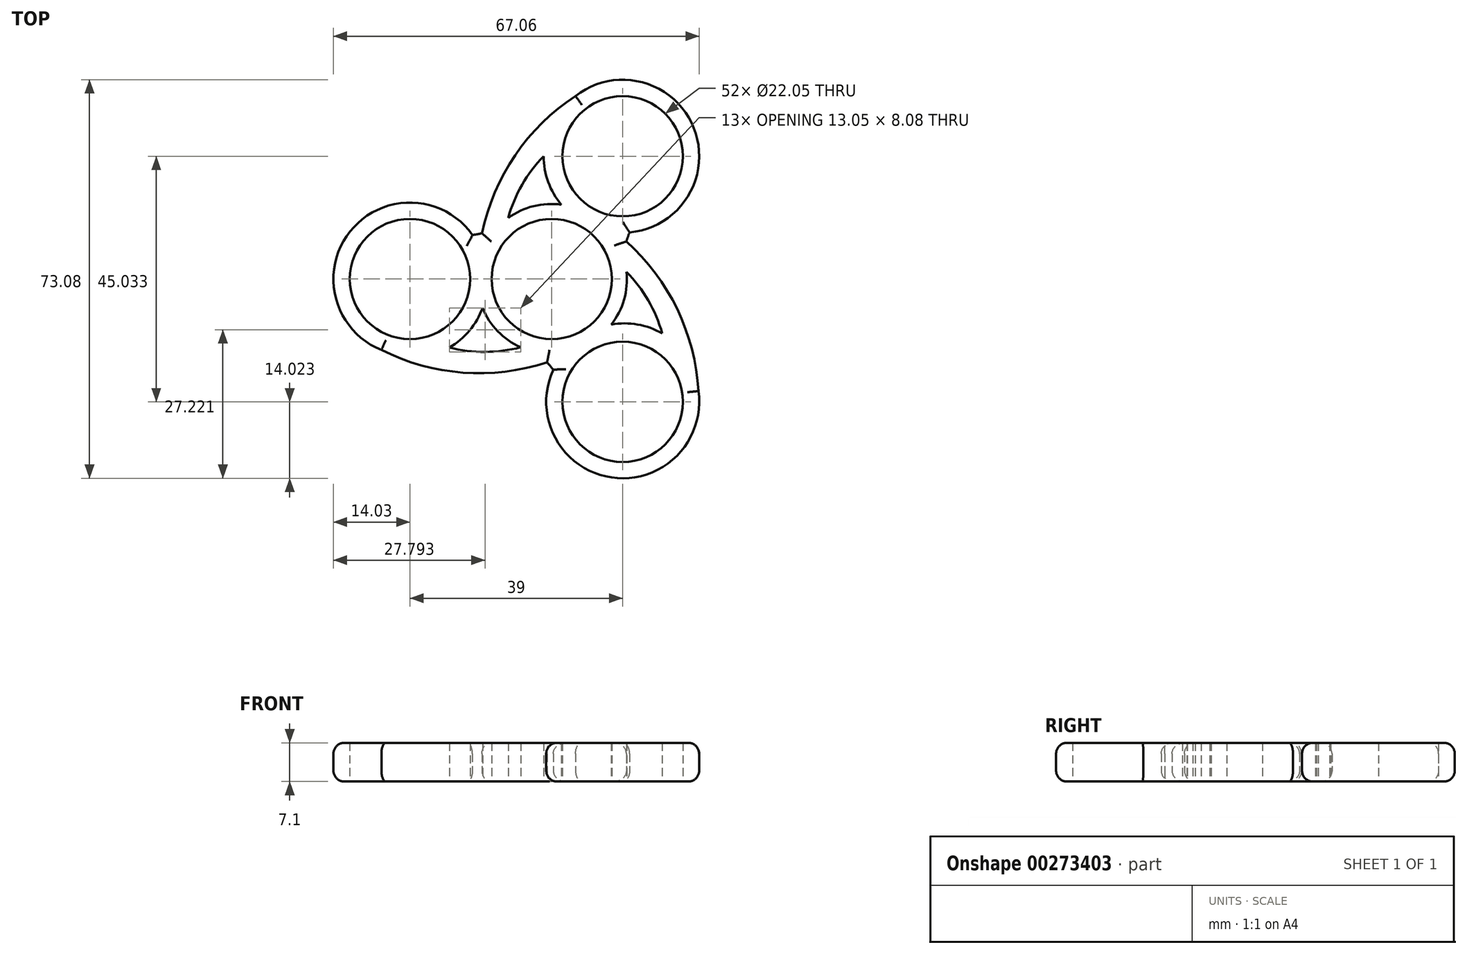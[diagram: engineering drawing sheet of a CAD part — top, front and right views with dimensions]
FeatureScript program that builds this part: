
annotation { "Feature Type Name" : "Feature", "Feature Type Description" : "" }
export const myFeature = defineFeature(function(context is Context, id is Id, definition is map)
    precondition{}
    {
        {
            var Q0;
            Q0=qCreatedBy(makeId("Top.planeOp"),FACE);
            var sketch = newSketch(context, id + "F0", { "sketchPlane" : qUnion([Q0])});
            skCircle(sketch, "E0", {"center": v(0, 0) * mm, "radius": 11.03 * mm});
            skCircle(sketch, "E1", {"center": v(13, 22.52) * mm, "radius": 11.03 * mm});
            skLineSegment(sketch, "E2", {"start": v(0, 0) * mm, "end": v(13, 22.52) * mm, "construction": true});
            skArc(sketch, "E3", {"start": v(14.28, 8.55) * mm, "mid": v(26.03, 27.7) * mm, "end": v(4.35, 33.55) * mm});
            skLineSegment(sketch, "E4", {"start": v(13, 22.52) * mm, "end": v(0.85, 29.53) * mm, "construction": true});
            skPoint(sketch, "E5.visualSharp", {"position": v(5.99, 10.37) * mm});
            skLineSegment(sketch, "E6", {"start": v(13, 22.52) * mm, "end": v(25.15, 15.5) * mm, "construction": true});
            skCircle(sketch, "E7", {"center": v(0, 0) * mm, "radius": 11.36 * mm, "construction": true});
            skPoint(sketch, "E8.center", {"position": v(-0.23, 0.06) * mm});
            skPoint(sketch, "E9.orphan", {"position": v(-5.27, 14.87) * mm});
            skPoint(sketch, "E10.orphan", {"position": v(7.2, 12.48) * mm});
            skPoint(sketch, "E11.1.5", {"position": v(0.06, -0.23) * mm});
            skPoint(sketch, "E11.2.5", {"position": v(0.17, 0.17) * mm});
            skArc(sketch, "E12", {"start": v(14.28, 8.55) * mm, "mid": v(13.95, 7.73) * mm, "end": v(13.68, 6.88) * mm});
            skArc(sketch, "E13.1.1", {"start": v(4.35, 33.55) * mm, "mid": v(-6.72, 22.68) * mm, "end": v(-12.8, 8.41) * mm});
            skCircle(sketch, "E14.1.1", {"center": v(-26, 0) * mm, "radius": 11.03 * mm});
            skArc(sketch, "E14.1.6", {"start": v(-31.23, -13.01) * mm, "mid": v(-16.28, -17.16) * mm, "end": v(-0.88, -15.3) * mm});
            skArc(sketch, "E14.1.7", {"start": v(-14.54, 8.09) * mm, "mid": v(-13.67, 8.21) * mm, "end": v(-12.8, 8.41) * mm});
            skLineSegment(sketch, "E14.1.8", {"start": v(-26, 0) * mm, "end": v(-26, 14.03) * mm, "construction": true});
            skLineSegment(sketch, "E14.1.9", {"start": v(-26, 0) * mm, "end": v(-26, -14.02) * mm, "construction": true});
            skPoint(sketch, "E14.1.10", {"position": v(-14.4, 0) * mm});
            skPoint(sketch, "E14.1.11", {"position": v(-10.25, -12) * mm});
            skPoint(sketch, "E14.1.12", {"position": v(-11.98, 0) * mm});
            skArc(sketch, "E14.1.13", {"start": v(-14.54, 8.09) * mm, "mid": v(-37, 8.7) * mm, "end": v(-31.23, -13.01) * mm});
            skCircle(sketch, "E14.2.1", {"center": v(13, -22.52) * mm, "radius": 11.03 * mm});
            skArc(sketch, "E14.2.6", {"start": v(26.89, -20.54) * mm, "mid": v(23, -5.52) * mm, "end": v(13.68, 6.88) * mm});
            skArc(sketch, "E14.2.7", {"start": v(0.27, -16.64) * mm, "mid": v(-0.28, -15.94) * mm, "end": v(-0.88, -15.3) * mm});
            skLineSegment(sketch, "E14.2.8", {"start": v(13, -22.52) * mm, "end": v(0.85, -29.53) * mm, "construction": true});
            skLineSegment(sketch, "E14.2.9", {"start": v(13, -22.52) * mm, "end": v(25.15, -15.5) * mm, "construction": true});
            skPoint(sketch, "E14.2.10", {"position": v(7.2, -12.48) * mm});
            skPoint(sketch, "E14.2.11", {"position": v(15.52, -2.87) * mm});
            skPoint(sketch, "E14.2.12", {"position": v(5.99, -10.37) * mm});
            skArc(sketch, "E14.2.13", {"start": v(0.27, -16.64) * mm, "mid": v(10.97, -36.4) * mm, "end": v(26.89, -20.54) * mm});
            skPoint(sketch, "E15.orphan", {"position": v(-13.6, -1.84) * mm});
            skPoint(sketch, "E16.orphan", {"position": v(8.4, -10.86) * mm});
            skArc(sketch, "E17.0", {"start": v(20.25, -9.97) * mm, "mid": v(17.69, -3.92) * mm, "end": v(13.7, 1.31) * mm});
            skArc(sketch, "E17.1", {"start": v(20.25, -9.97) * mm, "mid": v(15.73, -8.34) * mm, "end": v(10.92, -8.35) * mm});
            skArc(sketch, "E17.2", {"start": v(10.92, -8.35) * mm, "mid": v(13.25, -3.8) * mm, "end": v(13.7, 1.31) * mm});
            skArc(sketch, "E18.1.0", {"start": v(-1.49, 22.53) * mm, "mid": v(-0.65, 17.8) * mm, "end": v(1.77, 13.63) * mm});
            skArc(sketch, "E18.1.1", {"start": v(-1.49, 22.53) * mm, "mid": v(-5.45, 17.27) * mm, "end": v(-7.98, 11.2) * mm});
            skArc(sketch, "E18.1.2", {"start": v(1.77, 13.63) * mm, "mid": v(-3.34, 13.37) * mm, "end": v(-7.98, 11.2) * mm});
            skArc(sketch, "E18.2.0", {"start": v(-18.76, -12.55) * mm, "mid": v(-15.08, -9.45) * mm, "end": v(-12.7, -5.28) * mm});
            skArc(sketch, "E18.2.1", {"start": v(-18.76, -12.55) * mm, "mid": v(-12.23, -13.36) * mm, "end": v(-5.7, -12.52) * mm});
            skArc(sketch, "E18.2.2", {"start": v(-12.7, -5.28) * mm, "mid": v(-9.9, -9.58) * mm, "end": v(-5.7, -12.52) * mm});
            skSolve(sketch);
        }
        {
            var Q0;
            Q0=makeQuery(id+"F0.imprint","IMPRINT",FACE,{"disambiguationData":[TD([[makeQuery(id+"F0.imprint","IMPRINT",EDGE,{"derivedFrom":sQuery(id+"F0.wireOp",EDGE,"ea44153e-c5e4-4200-878d-53ebf284e07f.1.0")}),-1.0]])]});
            var Q1;
            Q1=makeQuery(id+"F0.imprint","IMPRINT",FACE,{"disambiguationData":[TD([[makeQuery(id+"F0.imprint","IMPRINT",EDGE,{"derivedFrom":sQuery(id+"F0.wireOp",EDGE,"E0")}),-1.0]])]});
            var Q2;
            Q2=makeQuery(id+"F0.imprint","IMPRINT",FACE,{"disambiguationData":[TD([[makeQuery(id+"F0.imprint","IMPRINT",EDGE,{"derivedFrom":sQuery(id+"F0.wireOp",EDGE,"E1")}),-1.0]])]});
            var Q3;
            {var subQ0=sQuery(id+"F0.wireOp",EDGE,"zqQpl2xC-KShR-byGl-JfGq-b1LpVGurQPJH");Q3=makeQuery(id+"F0.imprint","IMPRINT",FACE,{"disambiguationData":[TD([[makeQuery(id+"F0.imprint","IMPRINT",EDGE,{"derivedFrom":subQ0}),-1.0]])]});}
            extrude(context, id + "F1", {"entities" : qUnion([Q0, Q1, Q2, Q3]), "depth" : 7.1 * mm});
        }
        {
            var Q0;
            Q0=makeQuery(id+"F1.opExtrude","CAP_EDGE",EDGE,{"disambiguationData":[OSD([sQuery(id+"F0.wireOp",EDGE,"E13.1.1")])],"isStart":false});
            var Q1;
            Q1=makeQuery(id+"F1.opExtrude","CAP_EDGE",EDGE,{"disambiguationData":[OSD([sQuery(id+"F0.wireOp",EDGE,"E3")])],"isStart":false});
            var Q2;
            Q2=makeQuery(id+"F1.opExtrude","CAP_EDGE",EDGE,{"disambiguationData":[OSD([sQuery(id+"F0.wireOp",EDGE,"E14.2.6")])],"isStart":false});
            var Q3;
            Q3=makeQuery(id+"F1.opExtrude","CAP_EDGE",EDGE,{"disambiguationData":[OSD([sQuery(id+"F0.wireOp",EDGE,"E14.2.13")])],"isStart":false});
            var Q4;
            Q4=makeQuery(id+"F1.opExtrude","CAP_EDGE",EDGE,{"disambiguationData":[OSD([sQuery(id+"F0.wireOp",EDGE,"E14.1.6")])],"isStart":false});
            var Q5;
            Q5=makeQuery(id+"F1.opExtrude","CAP_EDGE",EDGE,{"disambiguationData":[OSD([sQuery(id+"F0.wireOp",EDGE,"E14.1.13")])],"isStart":false});
            var Q6;
            Q6=makeQuery(id+"F1.opExtrude","CAP_EDGE",EDGE,{"disambiguationData":[OSD([sQuery(id+"F0.wireOp",EDGE,"E14.1.7")])],"isStart":false});
            var Q7;
            Q7=makeQuery(id+"F1.opExtrude","CAP_EDGE",EDGE,{"disambiguationData":[OSD([sQuery(id+"F0.wireOp",EDGE,"E14.2.7")])],"isStart":false});
            var Q8;
            Q8=makeQuery(id+"F1.opExtrude","CAP_EDGE",EDGE,{"disambiguationData":[OSD([sQuery(id+"F0.wireOp",EDGE,"E12")])],"isStart":false});
            var Q9;
            Q9=makeQuery(id+"F1.opExtrude","CAP_EDGE",EDGE,{"disambiguationData":[OSD([sQuery(id+"F0.wireOp",EDGE,"E14.1.13")])],"isStart":true});
            var Q10;
            Q10=makeQuery(id+"F1.opExtrude","CAP_EDGE",EDGE,{"disambiguationData":[OSD([sQuery(id+"F0.wireOp",EDGE,"E14.1.6")])],"isStart":true});
            var Q11;
            Q11=makeQuery(id+"F1.opExtrude","CAP_EDGE",EDGE,{"disambiguationData":[OSD([sQuery(id+"F0.wireOp",EDGE,"E14.2.13")])],"isStart":true});
            var Q12;
            Q12=makeQuery(id+"F1.opExtrude","CAP_EDGE",EDGE,{"disambiguationData":[OSD([sQuery(id+"F0.wireOp",EDGE,"E14.2.7")])],"isStart":true});
            var Q13;
            Q13=makeQuery(id+"F1.opExtrude","CAP_EDGE",EDGE,{"disambiguationData":[OSD([sQuery(id+"F0.wireOp",EDGE,"E14.2.6")])],"isStart":true});
            var Q14;
            Q14=makeQuery(id+"F1.opExtrude","CAP_EDGE",EDGE,{"disambiguationData":[OSD([sQuery(id+"F0.wireOp",EDGE,"E3")])],"isStart":true});
            var Q15;
            Q15=makeQuery(id+"F1.opExtrude","CAP_EDGE",EDGE,{"disambiguationData":[OSD([sQuery(id+"F0.wireOp",EDGE,"E12")])],"isStart":true});
            var Q16;
            Q16=makeQuery(id+"F1.opExtrude","CAP_EDGE",EDGE,{"disambiguationData":[OSD([sQuery(id+"F0.wireOp",EDGE,"E13.1.1")])],"isStart":true});
            var Q17;
            Q17=makeQuery(id+"F1.opExtrude","CAP_EDGE",EDGE,{"disambiguationData":[OSD([sQuery(id+"F0.wireOp",EDGE,"E14.1.7")])],"isStart":true});
            fillet(context, id + "F2", {"entities" : qUnion([Q0, Q1, Q2, Q3, Q4, Q5, Q6, Q7, Q8, Q9, Q10, Q11, Q12, Q13, Q14, Q15, Q16, Q17]), "radius" : 2 * mm, "allowEdgeOverflow" : false});
        }
    });
